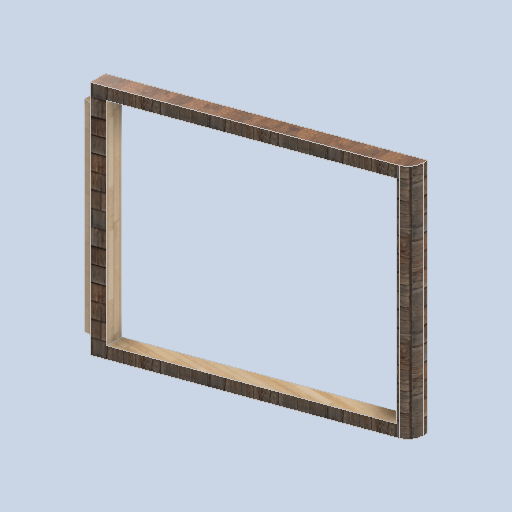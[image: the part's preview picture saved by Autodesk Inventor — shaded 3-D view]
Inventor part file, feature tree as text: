
AUTODESK INVENTOR PART (.ipt)
format: ipt  version: 2024.2 (Build 282272000, 272)  size: 193,536 bytes
history: native  units: in
note: dims shown in document units (in); Inventor stores cm internally (conversion verified against a paired STEP export)
features: sketch x5, other x3, plane x1
ambient origin geometry x8: Origin, YZ Plane, XZ Plane, XY Plane, X Axis, Y Axis, Z Axis, Center Point
bodies: Solid1 (feature_tree)
feature tree (9):
  other  "side_curve_frame_01_MIR.ipt"
  other  "Solid1::side_curve_frame_01_MIR.ipt"
  other  "TaggingFeature1"
  sketch  "Sketch1"  dims[d0=0.3937in]
  sketch  "Sketch2"
  sketch  "Sketch3"
  sketch  "Sketch4"
  sketch  "Sketch5"
  plane  "Work Plane1"
